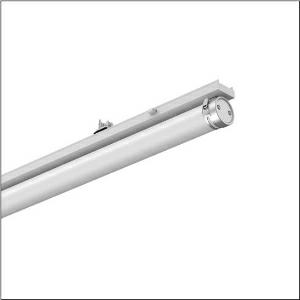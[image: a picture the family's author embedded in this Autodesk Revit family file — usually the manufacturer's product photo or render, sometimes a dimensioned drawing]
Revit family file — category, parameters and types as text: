
# Revit family: monsun_31_tube_51ft10mn4a0atr2
name_source: partatom
category: Lighting Fixtures
units: mm (PartAtom-declared; Revit-internal decimal feet)

## family parameters
Cut with Voids When Loaded = No
Host = Face
Light Source = No
Part Type = Normal
Room Calculation Point = No
Round Connector Dimension = Use Diameter
Shared = No

## types (1)
- --- (1 x LED, 10000 lm, 58 W, 4000K)
    Apparent Load = 58 VA
    CIE Flux Codes = 42 71 90 91 100
    Color Rendering = 80
    Color Temperature = 4000K
    Default Elevation = 1800 mm
    Description = Monsun 31 Tube, tubular luminaire, primary optical cover: diffuser, of PMMA, light emission: direct distribution, primary light characteristic: symmetric, LED, rated luminous flux: 10.000lm, luminous efficacy: 172lm/W, light colour: 840, colour temperature: 4000K, control gear: ON/OFF Multilumen, with with 1 terminal, 3-pole, max. 2.5mm², mains connection: 220..240V, AC, 50/60Hz, rated input power: 58W, housing, cylindrical, of PMMA, semi-transparent, matt white, with luminaire and ceiling fastening, V4A, mounting with brackets of stainless steel, length: 1.500mm, diameter: 75mm, end cap, of stainless steel (V4A), protection rating (complete): IP20, protection rating (lamp compartment): IP67/69K, insulation class (complete): insulation class I (protective earthing), certification: CE, UKCA, impact resistance: IK06, permissible operating ambient temperature: -20..+40°C, corresponds to IFS (International Featured Standards) requirements for safety and quality in the food industry, contact your sales advisor before using the luminaires in applications with unclear chemical exposure, large temperature fluctuations or condensation-forming humidity, packaging unit: 1 piece
    Height = 132 mm
    Lamp = 1 x LED
    Lamp Light Flux = 10000 lm
    Lamp Power = 58 W
    Lamp count = 1
    Length = 1500 mm
    Luminous efficacy = 172 lm/W
    Manufacturer = Siteco
    ModVariant = No
    Model = 51FT10MN4A0ATR2
    Mounting Place = Ceiling
    Mounting Type = Pendant
    Number of Poles = 1
    OnlyDefault = Yes
    Power Factor = 1
    Product Name = Monsun 31 Tube
    Product group = tubular luminaire
    ProductGroupID = 906
    Protection Class = Protection class I
    Protection Degree = IP 20
    RLX_Detail_Level = 1
    RLX_Emergency_Light_Flux = 0 lm
    RLX_Emergency_Type = 0
    RLX_Emergency_Type_DB = No
    RlxData = <blob elided: 32357 chars, md5=a41d321d>
    Socket = socket
    Standby Power = 0 W
    System Light Flux = 10000 lm
    System Power = 58 W
    Type Comments = factory setting: luminous flux: 100 % | (OFF | OFF | OFF | OFF) | 350 mA
    Type Image = l_1242814.jpg
    URL = http://relux.com
    VarID = @adj_142857
    Voltage = 0 V
    Weight = 0.00 kg
    Width = 79 mm

## geometry (parser evidence)
native form markers: Blend x4, Sweep x11
no freeform markers — native parametric forms only
